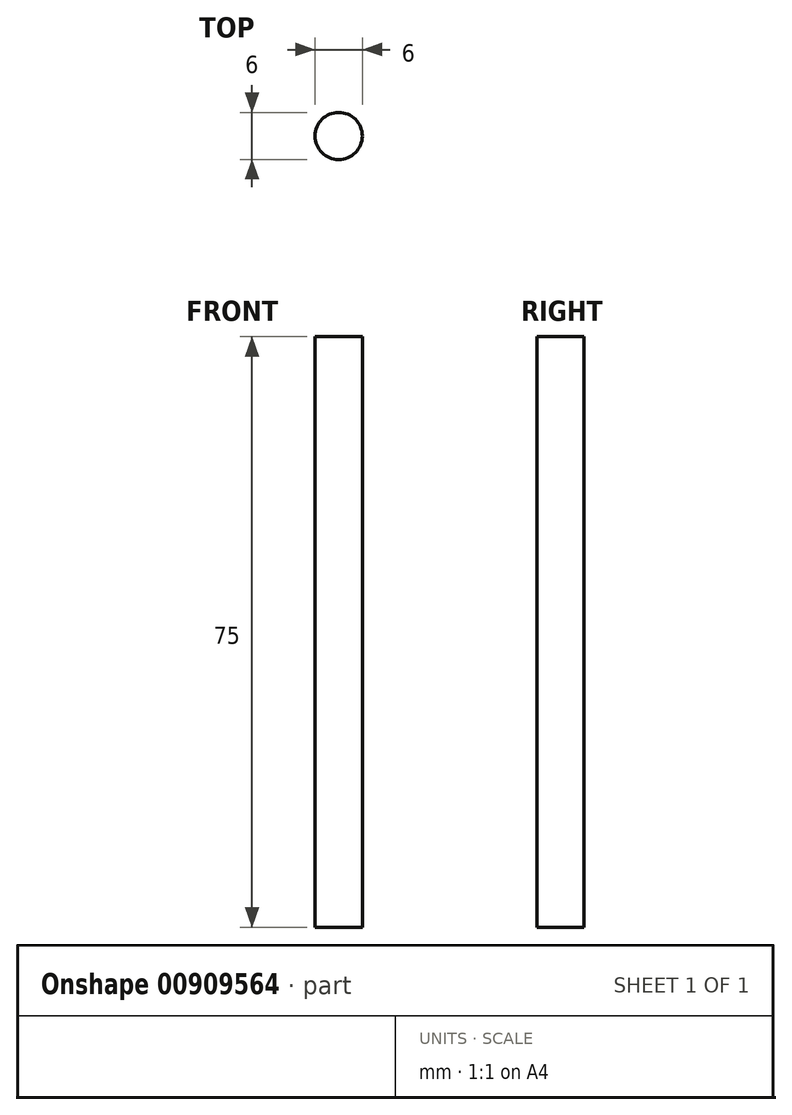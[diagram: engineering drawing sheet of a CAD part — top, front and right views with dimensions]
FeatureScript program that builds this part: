
annotation { "Feature Type Name" : "Feature", "Feature Type Description" : "" }
export const myFeature = defineFeature(function(context is Context, id is Id, definition is map)
    precondition{}
    {
        {
            var Q0;
            Q0=qCreatedBy(makeId("Top.planeOp"),FACE);
            var sketch = newSketch(context, id + "F0", { "sketchPlane" : qUnion([Q0])});
            skCircle(sketch, "E0", {"center": v(0, 0) * mm, "radius": 3 * mm});
            skSolve(sketch);
        }
        {
            var Q0;
            Q0 = qSketchRegion(id + "F0", true);
            extrude(context, id + "F1", {"entities" : qUnion([Q0]), "depth" : 75 * mm, "offsetDistance" : 25 * mm});
        }
    });
